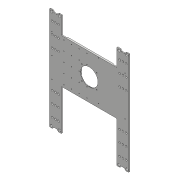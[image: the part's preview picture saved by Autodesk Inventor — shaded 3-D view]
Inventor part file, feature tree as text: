
AUTODESK INVENTOR PART (.ipt)
format: ipt  version: 2018 (Build 220112000, 112)  size: 477,696 bytes
history: native  units: mm
features: sketch x13, extrude x7, hole x6, fillet x6, mirror x5, projected_geometry x4, pattern_linear x2, chamfer x1
ambient origin geometry x8: Origin, YZ Plane, XZ Plane, XY Plane, X Axis, Y Axis, Z Axis, Center Point
bodies: Solid1 (feature_tree)
feature tree (44):
  extrude  "Extrusion1"  Depth=222.8mm
  hole  "Hole1"  [1 undecoded]
  mirror  "Mirror1"
  extrude  "Extrusion2"  Depth=64.56875mm
  extrude  "Extrusion3"  Depth=2.0mm
  mirror  "Mirror2"
  extrude  "Extrusion6"  Depth=6.1mm
  fillet  "Fillet1"  Radius=6.0mm
  hole  "Hole2"  [1 undecoded]
  pattern_linear  "Rectangular Pattern1"  Count1=2 Spacing1=7.0mm
  mirror  "Mirror4"
  mirror  "Mirror5"
  extrude  "Extrusion4"  Depth=1.5mm TaperAngle=0.0deg
  chamfer  "Chamfer1"  Distance=1.5mm Angle=45.0deg
  fillet  "Fillet2"  Radius=3.0mm
  hole  "Hole3"  [1 undecoded]
  hole  "Hole4"  [1 undecoded]
  pattern_linear  "Rectangular Pattern2"  Spacing1=28.4mm  [1 undecoded]
  hole  "Hole5"  [1 undecoded]
  mirror  "Mirror6"
  fillet  "Fillet3"  Radius=50.0mm
  hole  "Hole6"  [1 undecoded]
  extrude  "Extrusion7"  Depth=0.5mm
  fillet  "Fillet4"  Radius=16.666667mm
  fillet  "Fillet5"  Radius=6.0mm
  extrude  "Extrusion8"  Depth=0.5mm
  fillet  "Fillet6"  Radius=5.0mm
  sketch  "Sketch1"  dims[d0=172.0mm d1=222.8mm]
  sketch  "Sketch2"  dims[d2=2.0mm d3=0.0mm d4=214.7248mm]
  sketch  "Sketch3"  dims[d5=17.4625mm d6=64.56875mm]
  sketch  "Sketch4"  dims[d7=5.3mm d8=6.0mm d9=10.4mm d10=2.0mm d11=90.0deg d12=8.0mm d13=20.594885mm d14=5.1mm]
  sketch  "Sketch5"  dims[d15=5.1mm d16=6.1mm d17=6.0mm]
  sketch  "Sketch6"  dims[d18=2.0mm d19=0.0mm d20=120.0mm]
  sketch  "Sketch7"  dims[d21=88.8mm]
  projected_geometry  "Projected Loop1"
  sketch  "Sketch9"  dims[d22=2.0mm d23=0.0mm]
  sketch  "Sketch10"  dims[d24=1.0mm d25=1.0mm]
  sketch  "Sketch11"  dims[d26=50.8mm]
  sketch  "Sketch12"  dims[d28=12.7mm]
  projected_geometry  "Projected Loop2"
  sketch  "Sketch13"  dims[d29=4.3mm d30=6.0mm d31=9.4mm d32=2.0mm d33=90.0deg d34=8.0mm d35=20.594885mm d36=20.0mm d38=7.0mm]
  projected_geometry  "Projected Loop3"
  sketch  "Sketch14"  dims[d39=20.0mm d41=7.0mm d43=1.5mm d44=0.0mm d45=1.5mm d46=2.0mm d47=45.0deg d48=3.0mm d49=58.0mm d50=86.0mm d51=1.567mm d52=4.0mm d53=4.4mm d54=2.0mm d55=90.0deg d56=6.3mm d57=20.594885mm d58=28.4mm d59=8.0mm d62=50.0mm d63=16.666667mm d64=16.666667mm d65=16.666667mm d66=6.0mm d67=1.567mm d68=4.0mm d69=4.4mm d70=2.0mm d71=90.0deg d72=6.3mm d73=20.594885mm d74=50.0mm d76=21.0mm d77=5.0mm d78=90.0mm d79=5.0mm d80=1.567mm d81=4.0mm d82=4.4mm d83=2.0mm d84=90.0deg d85=6.3mm d86=20.594885mm d87=120.0mm d88=38.0mm d89=10.0mm d90=0.0mm d91=100.0mm d92=25.4mm d93=2.0mm d94=42.0624mm d95=32.0mm d96=32.0mm d97=2.459mm d98=6.0mm d99=6.3mm d100=2.0mm d101=90.0deg d102=8.8mm d103=20.594885mm d104=40.5mm d105=40.5mm d106=2.0mm d107=0.0mm d108=1.0mm d109=0.5mm d110=38.0mm d111=3.0mm d112=0.0mm d113=0.5mm]
  projected_geometry  "Projected Loop4"
note: 7 required parameter values undecoded (feature->parameter linkage not recoverable at this tier; creation-order binding heuristic only, values carry confidence <= 0.55)
